# Revit family: Stainless_Steel_Shelf-Wall_Mounted-Bobrick-298_Series
name_source: partatom
category: Plumbing Fixtures
revit_build: Autodesk Revit 2016 (Build: 20150714_1515(x64)
units: mm (PartAtom-declared; Revit-internal decimal feet)

## family parameters
Cut with Voids When Loaded = No
Host = Face
Part Type = Normal
Room Calculation Point = No
Round Connector Dimension = Use Diameter
Shared = Yes

## types (2) — shared parameters
ADA Compliant = Yes
CW Connection = No
Default Elevation = 40"
Description = Shelf shall be type-304, 18-gauge (1.2mm) stainless steel with satin finish. Mounting brackets, welded to shelf.
HW Connection = No
Height = 3"
Installation Type = Wall Mounted
Manufacturer = Bobrick
Material = Stainless Steel, Satin Finish
Model = B-298
Price = Prices may vary. Please consult Manufacturer Representative for most up-to-date price list.
Product Documentation Link = http://bobrick.com
Product Page URL = http://bobrick.com
URL = http://bobrick.com
Vent Connection = No
Warranty Information = 3 Years Warranty
Waste Connection = No
Width = 8"
zero-valued in all types: CWFU, HWFU, WFU

## per-type parameters (varying)
| type | Length |
| B-298x18 | 18" |
| B-298x24 | 24" |

## geometry (parser evidence)
native form markers: Sweep x3
no freeform markers — native parametric forms only
